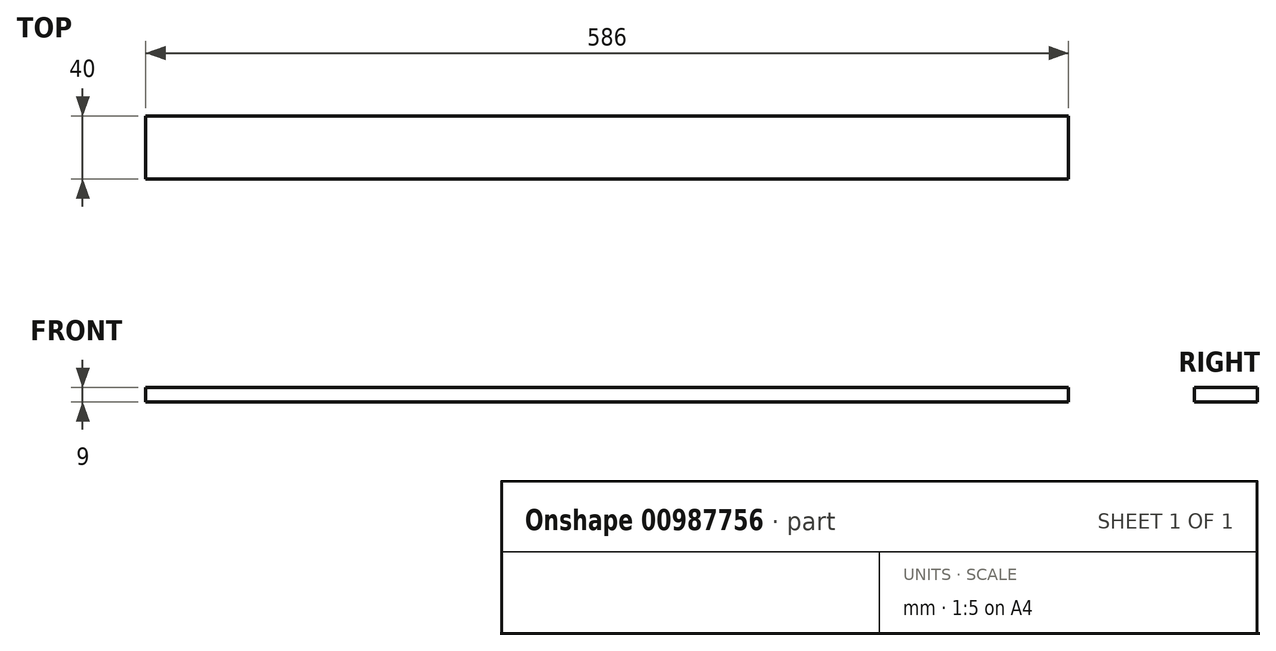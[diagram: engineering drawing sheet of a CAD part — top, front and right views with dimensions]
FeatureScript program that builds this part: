
annotation { "Feature Type Name" : "Feature", "Feature Type Description" : "" }
export const myFeature = defineFeature(function(context is Context, id is Id, definition is map)
    precondition{}
    {
        {
            var Q0;
            Q0=qCreatedBy(makeId("Right.planeOp"),FACE);
            var sketch = newSketch(context, id + "F0", { "sketchPlane" : qUnion([Q0])});
            skLineSegment(sketch, "E0.bottom", {"start": v(-20, -4.5) * mm, "end": v(20, -4.5) * mm});
            skLineSegment(sketch, "E0.top", {"start": v(-20, 4.5) * mm, "end": v(20, 4.5) * mm});
            skLineSegment(sketch, "E0.left", {"start": v(-20, -4.5) * mm, "end": v(-20, 4.5) * mm});
            skLineSegment(sketch, "E0.right", {"start": v(20, -4.5) * mm, "end": v(20, 4.5) * mm});
            skPoint(sketch, "E0.middle", {"position": v(0, 0) * mm});
            skSolve(sketch);
        }
        {
            var Q0;
            Q0=qSketchRegion(id+"F0",true);
            extrude(context, id + "F1", {"entities" : qUnion([Q0]), "endBound" : BoundingType.SYMMETRIC, "oppositeDirection" : true, "depth" : 586 * mm, "offsetDistance" : 25 * mm});
        }
    });
